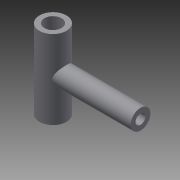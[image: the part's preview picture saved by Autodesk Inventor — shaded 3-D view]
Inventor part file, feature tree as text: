
AUTODESK INVENTOR PART (.ipt)
format: ipt  version: 2014 (Build 180170000, 170)  size: 1,338,368 bytes
history: native  units: mm
features: sketch x3, extrude x2, plane x2, emboss x1
ambient origin geometry x8: Origin, YZ Plane, XZ Plane, XY Plane, X Axis, Y Axis, Z Axis, Center Point
bodies: Solid1 (feature_tree)
feature tree (8):
  extrude  "Extrusion1"  Depth=22.0472mm
  plane  "Work Plane1"
  extrude  "Extrusion3"  Depth=11.2776mm
  plane  "Work Plane2"
  emboss  "Emboss1"
  sketch  "Sketch1"  dims[d0=34.7472mm d1=22.0472mm]
  sketch  "Sketch2"  dims[d2=101.6mm d3=0.0mm d4=11.2776mm]
  sketch  "Sketch7"  dims[d5=25.4mm d8=12.7mm d9=101.6mm d10=0.0mm d11=-21.5mm d13=4.0mm d14=1.0mm d15=0.0mm]
